# Revit family: Grohe_PlumbingFixtures_Eurosmart_SingleLeverBasinMixer_23975003xxxxxx
name_source: partatom
category: Plumbing Fixtures
revit_build: Autodesk Revit 2018 (Build: 20190510_1515(x64)
units: mm (PartAtom-declared; Revit-internal decimal feet)

## family parameters
Cut with Voids When Loaded = No
Host = Face
OmniClass Number = 23.65.00.00
OmniClass Title = Supply and Distribution of Liquids and Gases
Part Type = Normal
Room Calculation Point = No
Round Connector Dimension = Use Diameter
Shared = No

## types (1)
- 23975003
    Assembly Code = D2010
    AssetType = Fixed
    BIMObjectName = Grohe_PlumbingFixtures_Eurosmart_SingleLeverBasinMixer_23975003
    CO2NeutralProduction = GROHE is one of the first leading manufacturer within the sanitary industry having a CO2-neutral production.
    CW Connection = Yes
    CWFU = 0
    ClassificationName = Uniclass 2015
    ClassificationValue = Pr_40_20_87_55
    Color = Chrome
    Default Elevation = 0 mm  [stored 0 ft]
    Description = Eurosmart single-lever basin mixer
    DocumentationCertificates = https://www.bimstore.co
    DocumentationInstallationGuide = https://www.bimstore.co
    DocumentationLiterature = https://www.bimstore.co
    DocumentationMaintenance = https://www.bimstore.co
    DocumentationTechnical = https://www.bimstore.co
    DurationUnit = Year
    EF000003 = Top/tap hole
    EF000139 = Chromium-plated
    EF000278 = 0
    EF000332 = 0 mm  [stored 0 ft]
    EF000846 = 0 mm  [stored 0 ft]
    EF000958 = 0
    EF001469 = Battery
    EF002149 = 0
    EF002286 = Hose (gland nut)
    EF002671 = Chrome
    EF003625 = 6
    EF004121 = 0
    EF005464 = 0
    EF005474 = IP59K
    EF006013 = 0
    EF006974 = Manually operated
    EF007955 = 0
    EF011781 = 0
    EF012635 = 0
    EF012637 = 0
    EF014578 = 0
    EF014591 = 0
    EF020103 = 0
    EF020776 = 0
    EF020779 = 0
    EF020785 = 3/8 inch
    EF020788 = 0
    EF020789 = 122 mm
    EF020791 = Brass
    EF020794 = 0
    EF020795 = Fixed, bottom
    EF020796 = 158 mm
    EF020797 = 138 mm
    EF020800 = 0
    EF020801 = 0
    EF020825 = 0
    EF020826 = 0
    EF020871 = 0
    EF020872 = 0
    EF020873 = 0
    EF020966 = 0
    EF021720 = 0
    EF021808 = 1-hole
    EF021835 = 0 mm  [stored 0 ft]
    EF021836 = 0
    EF022117 = Infrared
    EF022133 = 0
    EF022232 = 0
    EF022750 = Cast
    EF023686 = 0
    EF023688 = Foam jet nozzle
    EF023957 = 0
    EF024921 = 0
    EF024922 = 4 - 80
    EF025098 = 0
    EF025099 = 30 - 600
    EF025101 = 0
    EF025102 = Remote control
    EF025109 = Polished
    EF025247 = 0
    EFDE0022 = Group I, <=20 dB(A)
    EFNL0001 = 0
    EFSE0002 = 0
    Ecojoy = No
    ExpectedLife = 0
    Features = Single hole installation; 2-in-1 hybrid with touchless or manual operation; manual lever operation having priority; GROHE SilkMove 28 mm ceramic cartridge; with temperature limiter; infra-red electronic; with infrared sensor for bi-directional communication for monitoring, configuration and service purpose; 6V lithium battery, type CR-P2; battery lifetime: approx. 7 years (150 actuations a day); non-return valve; dirt strainers; integrated solenoid valve; external battery; multistage battery status display; 7 pre-set programs; auto flush; cleaning mode; additional functions and precise settings by remote control 36 407; GROHE StarLight chrome finish; GROHE EcoJoy mousseur 5.7 l/min; GROHE Zero isolated inner water ways - lead and nickel free within the faucet; rapid installation system; smooth body; flexible connection hoses; minimum pressure 1.0 bar; CE approved.
    FullRecyclabilityOfPlastic = All plastic components are fully recyclable
    GROHESocialCommittment = green.grohe.com/social_engagement
    GROHESustainability = green.grohe.com
    HW Connection = Yes
    HWFU = 0
    IfcExportAs = IfcPipeFitting
    IfcExportType = IfcPipeFittingType
    Keynote = N13
    Manufacturer = Grohe
    ManufacturerName = Grohe
    Model = 23975003
    ModelNumber = 23975003
    ModelReference = Single-Lever Basin Mixer 1/2″ M-Size
    NBSDescription = Mixer taps
    NBSObjectName = Grohe - Mixer taps
    NBSReference = 45-35-70/345
    NominalDepth = 0 mm  [stored 0 ft]
    NominalHeight = 0 mm  [stored 0 ft]
    NominalLength = 0 mm  [stored 0 ft]
    PrimaryMaterial = Steel, Chrome Plated
    ProductionYear = 2021
    SustainabilityAward = green.grohe.com/awards
    SustainabilityReport = green.grohe.com/reporting
    Type Comments = Single-Lever Basin Mixer 1/2″ M-Size
    TypeName = Single-Lever Basin Mixer 1/2″ M-Size
    URL = https://www.grohe.co.uk
    Vent Connection = No
    WFU = 0
    WarrantyDurationLabor = 0
    WarrantyDurationParts = 0
    WarrantyDurationUnit = Year
    Waste Connection = No
    _BSBibleVersion = 16
    _BimSpecGuid = 0
    _CurrentRevision = 1
    _DistributedBy = www.bimstore.co
    _ObjectUserGuide = https://www.bimstore.co

note: [stored X ft] marks values corroborated as IEEE doubles in the binary element streams (Revit-internal decimal feet)

## geometry (parser evidence)
native form markers: Sweep x3
no freeform markers — native parametric forms only
